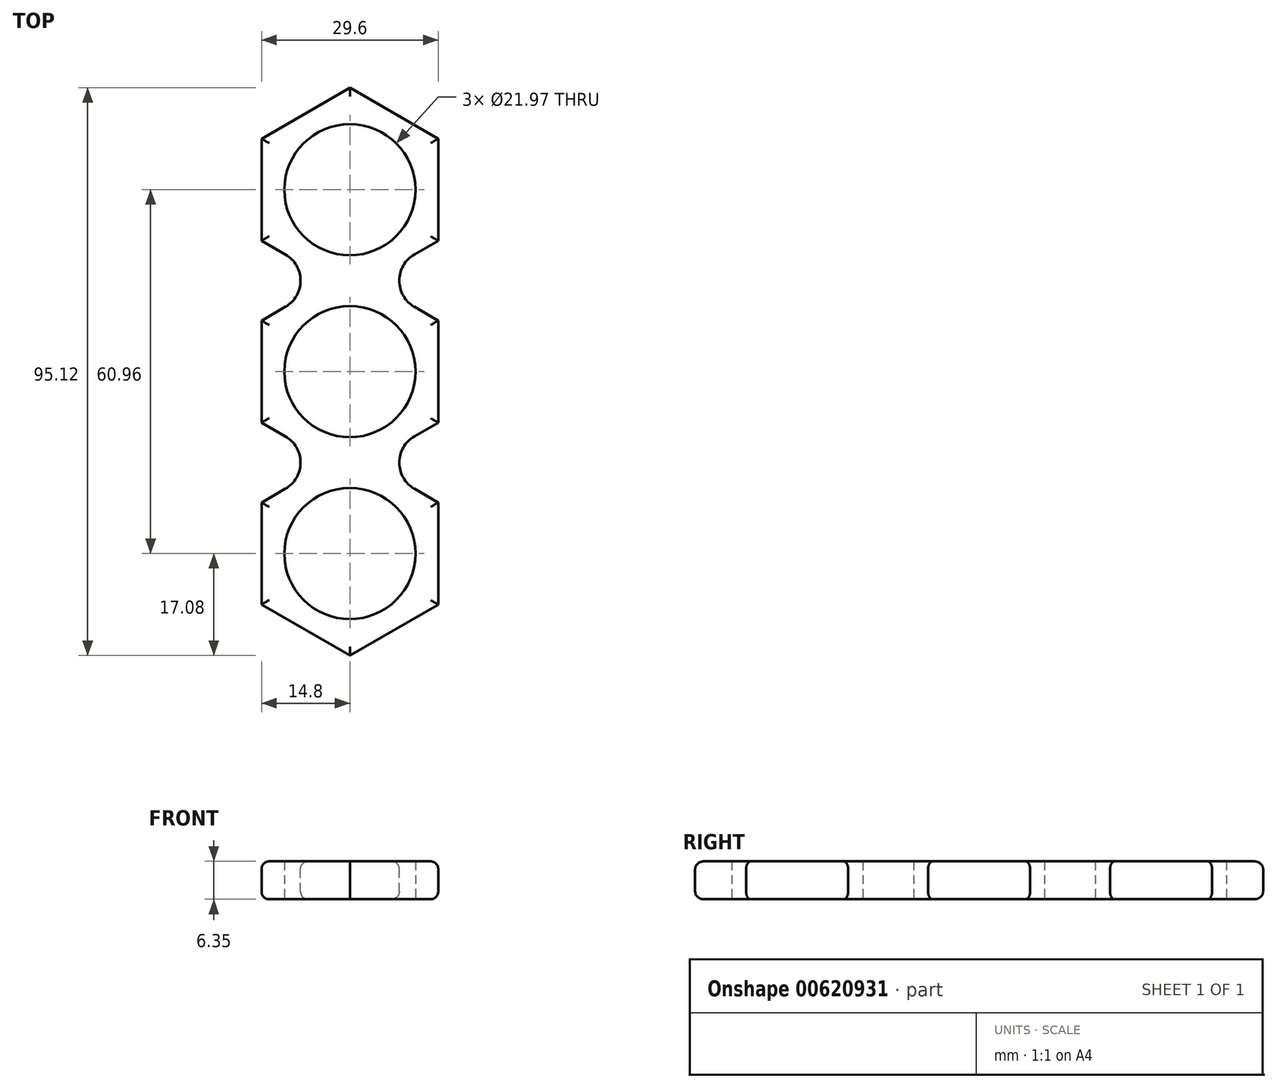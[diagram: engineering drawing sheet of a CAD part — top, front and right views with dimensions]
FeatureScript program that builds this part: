
annotation { "Feature Type Name" : "Feature", "Feature Type Description" : "" }
export const myFeature = defineFeature(function(context is Context, id is Id, definition is map)
    precondition{}
    {
        {
            var Q0;
            Q0=qCreatedBy(makeId("Top.planeOp"),FACE);
            var sketch = newSketch(context, id + "F0", { "sketchPlane" : qUnion([Q0])});
            skCircle(sketch, "E0", {"center": v(0, 0) * mm, "radius": 10.99 * mm});
            skCircle(sketch, "E1", {"center": v(0, 30.48) * mm, "radius": 10.99 * mm});
            skCircle(sketch, "E2", {"center": v(0, -30.48) * mm, "radius": 10.99 * mm});
            skCircle(sketch, "E3", {"center": v(0, -30.48) * mm, "radius": 14.8 * mm});
            skCircle(sketch, "E4", {"center": v(0, 30.48) * mm, "radius": 14.8 * mm});
            skLineSegment(sketch, "E5", {"start": v(0, 0) * mm, "end": v(0, 30.48) * mm});
            skLineSegment(sketch, "E6", {"start": v(0, 0) * mm, "end": v(0, -30.48) * mm});
            skCircle(sketch, "E7", {"center": v(0, 0) * mm, "radius": 14.8 * mm});
            skCircle(sketch, "E8.cCircle", {"center": v(0, 30.48) * mm, "radius": 14.8 * mm, "construction": true});
            skLineSegment(sketch, "E8.0", {"start": v(14.8, 39.02) * mm, "end": v(14.8, 21.94) * mm});
            skLineSegment(sketch, "E8.1", {"start": v(14.8, 21.94) * mm, "end": v(0, 13.4) * mm});
            skLineSegment(sketch, "E8.2", {"start": v(0, 13.4) * mm, "end": v(-14.8, 21.94) * mm});
            skLineSegment(sketch, "E8.3", {"start": v(-14.8, 21.94) * mm, "end": v(-14.8, 39.02) * mm});
            skLineSegment(sketch, "E8.4", {"start": v(-14.8, 39.02) * mm, "end": v(0, 47.56) * mm});
            skLineSegment(sketch, "E8.5", {"start": v(0, 47.56) * mm, "end": v(14.8, 39.02) * mm});
            skPoint(sketch, "E8.0.midPoint", {"position": v(14.8, 30.48) * mm});
            skCircle(sketch, "E9.cCircle", {"center": v(0, 0) * mm, "radius": 14.8 * mm, "construction": true});
            skLineSegment(sketch, "E9.0", {"start": v(14.8, 8.54) * mm, "end": v(14.8, -8.54) * mm});
            skLineSegment(sketch, "E9.1", {"start": v(14.8, -8.54) * mm, "end": v(0, -17.08) * mm});
            skLineSegment(sketch, "E9.2", {"start": v(0, -17.08) * mm, "end": v(-14.8, -8.54) * mm});
            skLineSegment(sketch, "E9.3", {"start": v(-14.8, -8.54) * mm, "end": v(-14.8, 8.54) * mm});
            skLineSegment(sketch, "E9.4", {"start": v(-14.8, 8.54) * mm, "end": v(0, 17.08) * mm});
            skLineSegment(sketch, "E9.5", {"start": v(0, 17.08) * mm, "end": v(14.8, 8.54) * mm});
            skPoint(sketch, "E9.0.midPoint", {"position": v(14.8, 0) * mm});
            skCircle(sketch, "E10.cCircle", {"center": v(0, -30.48) * mm, "radius": 14.8 * mm, "construction": true});
            skLineSegment(sketch, "E10.0", {"start": v(14.8, -21.94) * mm, "end": v(14.8, -39.02) * mm});
            skLineSegment(sketch, "E10.1", {"start": v(14.8, -39.02) * mm, "end": v(0, -47.56) * mm});
            skLineSegment(sketch, "E10.2", {"start": v(0, -47.56) * mm, "end": v(-14.8, -39.02) * mm});
            skLineSegment(sketch, "E10.3", {"start": v(-14.8, -39.02) * mm, "end": v(-14.8, -21.94) * mm});
            skLineSegment(sketch, "E10.4", {"start": v(-14.8, -21.94) * mm, "end": v(0, -13.4) * mm});
            skLineSegment(sketch, "E10.5", {"start": v(0, -13.4) * mm, "end": v(14.8, -21.94) * mm});
            skPoint(sketch, "E10.0.midPoint", {"position": v(14.8, -30.48) * mm});
            skSolve(sketch);
        }
        {
            var Q0;
            Q0 = qSketchRegion(id + "F0", true);
            var Q1;
            {var subQ0=sQuery(id+"F0.wireOp",EDGE,"E5");var subQ3=sQuery(id+"F0.wireOp",EDGE,"E0");var subQ4=makeQuery(id+"F0.imprint","INTERSECT",VERTEX,{"derivedFrom":[subQ3,subQ0]});Q1=makeQuery(id+"F0.imprint","IMPRINT",FACE,{"disambiguationData":[TD([[makeQuery(id+"F0.imprint","IMPRINT",EDGE,{"disambiguationData":[TD([[subQ4,1.0]])],"derivedFrom":subQ3}),-1.0]])]});}
            var Q2;
            {var subQ7=sQuery(id+"F0.wireOp",EDGE,"E0");var subQ11=sQuery(id+"F0.wireOp",EDGE,"E5");var subQ12=makeQuery(id+"F0.imprint","INTERSECT",VERTEX,{"derivedFrom":[subQ7,subQ11]});Q2=makeQuery(id+"F0.imprint","IMPRINT",FACE,{"disambiguationData":[TD([[makeQuery(id+"F0.imprint","IMPRINT",EDGE,{"disambiguationData":[TD([[subQ12,-1.0]])],"derivedFrom":subQ7}),-1.0]])]});}
            var Q3;
            {var subQ0=sQuery(id+"F0.wireOp",EDGE,"E9.4");var subQ1=sQuery(id+"F0.wireOp",EDGE,"E4");var subQ2=makeQuery(id+"F0.imprint","INTERSECT",VERTEX,{"derivedFrom":[subQ1,subQ0]});Q3=makeQuery(id+"F0.imprint","IMPRINT",FACE,{"disambiguationData":[TD([[makeQuery(id+"F0.imprint","IMPRINT",EDGE,{"disambiguationData":[TD([[subQ2,-1.0]])],"derivedFrom":subQ1}),1.0]])]});}
            var Q4;
            {var subQ0=sQuery(id+"F0.wireOp",EDGE,"E5");var subQ1=sQuery(id+"F0.wireOp",EDGE,"E4");var subQ2=makeQuery(id+"F0.imprint","INTERSECT",VERTEX,{"derivedFrom":[subQ1,subQ0]});Q4=makeQuery(id+"F0.imprint","IMPRINT",FACE,{"disambiguationData":[TD([[makeQuery(id+"F0.imprint","IMPRINT",EDGE,{"disambiguationData":[TD([[subQ2,-1.0]])],"derivedFrom":subQ1}),1.0]])]});}
            var Q5;
            {var subQ1=sQuery(id+"F0.wireOp",EDGE,"E5");var subQ3=sQuery(id+"F0.wireOp",EDGE,"E7");var subQ4=makeQuery(id+"F0.imprint","INTERSECT",VERTEX,{"derivedFrom":[subQ1,subQ3]});Q5=makeQuery(id+"F0.imprint","IMPRINT",FACE,{"disambiguationData":[TD([[makeQuery(id+"F0.imprint","IMPRINT",EDGE,{"disambiguationData":[TD([[subQ4,-1.0]])],"derivedFrom":subQ3}),1.0]])]});}
            var Q6;
            {var subQ1=sQuery(id+"F0.wireOp",EDGE,"E5");var subQ3=sQuery(id+"F0.wireOp",EDGE,"E7");var subQ4=makeQuery(id+"F0.imprint","INTERSECT",VERTEX,{"derivedFrom":[subQ1,subQ3]});Q6=makeQuery(id+"F0.imprint","IMPRINT",FACE,{"disambiguationData":[TD([[makeQuery(id+"F0.imprint","IMPRINT",EDGE,{"disambiguationData":[TD([[subQ4,1.0]])],"derivedFrom":subQ3}),1.0]])]});}
            var Q7;
            {var subQ0=sQuery(id+"F0.wireOp",EDGE,"E9.1");var subQ1=sQuery(id+"F0.wireOp",EDGE,"E3");var subQ2=makeQuery(id+"F0.imprint","INTERSECT",VERTEX,{"derivedFrom":[subQ1,subQ0]});Q7=makeQuery(id+"F0.imprint","IMPRINT",FACE,{"disambiguationData":[TD([[makeQuery(id+"F0.imprint","IMPRINT",EDGE,{"disambiguationData":[TD([[subQ2,-1.0]])],"derivedFrom":subQ1}),1.0]])]});}
            var Q8;
            {var subQ1=sQuery(id+"F0.wireOp",EDGE,"E6");var subQ3=sQuery(id+"F0.wireOp",EDGE,"E7");var subQ4=makeQuery(id+"F0.imprint","INTERSECT",VERTEX,{"derivedFrom":[subQ1,subQ3]});Q8=makeQuery(id+"F0.imprint","IMPRINT",FACE,{"disambiguationData":[TD([[makeQuery(id+"F0.imprint","IMPRINT",EDGE,{"disambiguationData":[TD([[subQ4,-1.0]])],"derivedFrom":subQ3}),1.0]])]});}
            var Q9;
            {var subQ1=sQuery(id+"F0.wireOp",EDGE,"E6");var subQ3=sQuery(id+"F0.wireOp",EDGE,"E7");var subQ4=makeQuery(id+"F0.imprint","INTERSECT",VERTEX,{"derivedFrom":[subQ1,subQ3]});Q9=makeQuery(id+"F0.imprint","IMPRINT",FACE,{"disambiguationData":[TD([[makeQuery(id+"F0.imprint","IMPRINT",EDGE,{"disambiguationData":[TD([[subQ4,1.0]])],"derivedFrom":subQ3}),1.0]])]});}
            var Q10;
            {var subQ0=sQuery(id+"F0.wireOp",EDGE,"E6");var subQ1=sQuery(id+"F0.wireOp",EDGE,"E3");var subQ2=makeQuery(id+"F0.imprint","INTERSECT",VERTEX,{"derivedFrom":[subQ1,subQ0]});Q10=makeQuery(id+"F0.imprint","IMPRINT",FACE,{"disambiguationData":[TD([[makeQuery(id+"F0.imprint","IMPRINT",EDGE,{"disambiguationData":[TD([[subQ2,-1.0]])],"derivedFrom":subQ1}),1.0]])]});}
            extrude(context, id + "F1", {"entities" : qUnion([Q0, Q1, Q2, Q3, Q4, Q5, Q6, Q7, Q8, Q9, Q10]), "depth" : 6.35 * mm, "offsetDistance" : 25.4 * mm});
        }
        {
            var Q0;
            Q0=makeQuery(id+"F1.opExtrude","SWEPT_EDGE",EDGE,{"disambiguationData":[OSD([sQuery(id+"F0.wireOp",EDGE,"E8.2"),sQuery(id+"F0.wireOp",EDGE,"E9.4")])]});
            var Q1;
            Q1=makeQuery(id+"F1.opExtrude","SWEPT_EDGE",EDGE,{"disambiguationData":[OSD([sQuery(id+"F0.wireOp",EDGE,"E9.2"),sQuery(id+"F0.wireOp",EDGE,"E10.4")])]});
            var Q2;
            Q2=makeQuery(id+"F1.opExtrude","SWEPT_EDGE",EDGE,{"disambiguationData":[OSD([sQuery(id+"F0.wireOp",EDGE,"E9.1"),sQuery(id+"F0.wireOp",EDGE,"E10.5")])]});
            var Q3;
            Q3=makeQuery(id+"F1.opExtrude","SWEPT_EDGE",EDGE,{"disambiguationData":[OSD([sQuery(id+"F0.wireOp",EDGE,"E8.1"),sQuery(id+"F0.wireOp",EDGE,"E9.5")])]});
            fillet(context, id + "F2", {"entities" : qUnion([Q0, Q1, Q2, Q3]), "radius" : 5.08 * mm, "tangentPropagation" : true, "allowEdgeOverflow" : false});
        }
        {
            var Q0;
            Q0=makeQuery(id+"F1.opExtrude","CAP_EDGE",EDGE,{"disambiguationData":[OSD([sQuery(id+"F0.wireOp",EDGE,"E8.3")])],"isStart":false});
            var Q1;
            Q1=makeQuery(id+"F1.opExtrude","CAP_EDGE",EDGE,{"disambiguationData":[OSD([sQuery(id+"F0.wireOp",EDGE,"E8.4")])],"isStart":false});
            var Q2;
            Q2=makeQuery(id+"F1.opExtrude","CAP_EDGE",EDGE,{"disambiguationData":[OSD([sQuery(id+"F0.wireOp",EDGE,"E8.5")])],"isStart":false});
            var Q3;
            Q3=makeQuery(id+"F1.opExtrude","CAP_EDGE",EDGE,{"disambiguationData":[OSD([sQuery(id+"F0.wireOp",EDGE,"E8.0")])],"isStart":false});
            var Q4;
            Q4=makeQuery(id+"F1.opExtrude","CAP_EDGE",EDGE,{"disambiguationData":[OSD([sQuery(id+"F0.wireOp",EDGE,"E8.1")])],"isStart":false});
            var Q5;
            Q5=makeQuery(id+"F1.opExtrude","CAP_EDGE",EDGE,{"disambiguationData":[OSD([sQuery(id+"F0.wireOp",EDGE,"E8.2")])],"isStart":false});
            var Q6;
            Q6=makeQuery(id+"F1.opExtrude","CAP_EDGE",EDGE,{"disambiguationData":[OSD([sQuery(id+"F0.wireOp",EDGE,"E9.5")])],"isStart":false});
            var Q7;
            Q7=makeQuery(id+"F1.opExtrude","CAP_EDGE",EDGE,{"disambiguationData":[OSD([sQuery(id+"F0.wireOp",EDGE,"E9.0")])],"isStart":false});
            var Q8;
            Q8=makeQuery(id+"F1.opExtrude","CAP_EDGE",EDGE,{"disambiguationData":[OSD([sQuery(id+"F0.wireOp",EDGE,"E9.1")])],"isStart":false});
            var Q9;
            Q9=makeQuery(id+"F1.opExtrude","CAP_EDGE",EDGE,{"disambiguationData":[OSD([sQuery(id+"F0.wireOp",EDGE,"E10.5")])],"isStart":false});
            var Q10;
            Q10=makeQuery(id+"F1.opExtrude","CAP_EDGE",EDGE,{"disambiguationData":[OSD([sQuery(id+"F0.wireOp",EDGE,"E10.0")])],"isStart":false});
            var Q11;
            Q11=makeQuery(id+"F1.opExtrude","CAP_EDGE",EDGE,{"disambiguationData":[OSD([sQuery(id+"F0.wireOp",EDGE,"E10.1")])],"isStart":false});
            var Q12;
            Q12=makeQuery(id+"F1.opExtrude","CAP_EDGE",EDGE,{"disambiguationData":[OSD([sQuery(id+"F0.wireOp",EDGE,"E10.2")])],"isStart":false});
            var Q13;
            Q13=makeQuery(id+"F1.opExtrude","CAP_EDGE",EDGE,{"disambiguationData":[OSD([sQuery(id+"F0.wireOp",EDGE,"E10.3")])],"isStart":false});
            var Q14;
            Q14=makeQuery(id+"F1.opExtrude","CAP_EDGE",EDGE,{"disambiguationData":[OSD([sQuery(id+"F0.wireOp",EDGE,"E10.4")])],"isStart":false});
            var Q15;
            Q15=makeQuery(id+"F1.opExtrude","CAP_EDGE",EDGE,{"disambiguationData":[OSD([sQuery(id+"F0.wireOp",EDGE,"E9.2")])],"isStart":false});
            var Q16;
            Q16=makeQuery(id+"F1.opExtrude","CAP_EDGE",EDGE,{"disambiguationData":[OSD([sQuery(id+"F0.wireOp",EDGE,"E9.3")])],"isStart":false});
            var Q17;
            Q17=makeQuery(id+"F1.opExtrude","CAP_EDGE",EDGE,{"disambiguationData":[OSD([sQuery(id+"F0.wireOp",EDGE,"E9.4")])],"isStart":false});
            fillet(context, id + "F3", {"entities" : qUnion([Q0, Q1, Q2, Q3, Q4, Q5, Q6, Q7, Q8, Q9, Q10, Q11, Q12, Q13, Q14, Q15, Q16, Q17]), "radius" : 1.27 * mm, "tangentPropagation" : true, "allowEdgeOverflow" : false});
        }
        {
            var Q0;
            Q0=makeQuery(id+"F1.opExtrude","CAP_EDGE",EDGE,{"disambiguationData":[OSD([sQuery(id+"F0.wireOp",EDGE,"E8.3")])],"isStart":true});
            var Q1;
            Q1=makeQuery(id+"F1.opExtrude","CAP_EDGE",EDGE,{"disambiguationData":[OSD([sQuery(id+"F0.wireOp",EDGE,"E8.4")])],"isStart":true});
            var Q2;
            Q2=makeQuery(id+"F1.opExtrude","CAP_EDGE",EDGE,{"disambiguationData":[OSD([sQuery(id+"F0.wireOp",EDGE,"E8.5")])],"isStart":true});
            var Q3;
            Q3=makeQuery(id+"F1.opExtrude","CAP_EDGE",EDGE,{"disambiguationData":[OSD([sQuery(id+"F0.wireOp",EDGE,"E8.0")])],"isStart":true});
            var Q4;
            Q4=makeQuery(id+"F1.opExtrude","CAP_EDGE",EDGE,{"disambiguationData":[OSD([sQuery(id+"F0.wireOp",EDGE,"E8.1")])],"isStart":true});
            var Q5;
            Q5=makeQuery(id+"F1.opExtrude","CAP_EDGE",EDGE,{"disambiguationData":[OSD([sQuery(id+"F0.wireOp",EDGE,"E8.2")])],"isStart":true});
            var Q6;
            Q6=makeQuery(id+"F1.opExtrude","CAP_EDGE",EDGE,{"disambiguationData":[OSD([sQuery(id+"F0.wireOp",EDGE,"E9.4")])],"isStart":true});
            var Q7;
            Q7=makeQuery(id+"F1.opExtrude","CAP_EDGE",EDGE,{"disambiguationData":[OSD([sQuery(id+"F0.wireOp",EDGE,"E9.5")])],"isStart":true});
            var Q8;
            Q8=makeQuery(id+"F1.opExtrude","CAP_EDGE",EDGE,{"disambiguationData":[OSD([sQuery(id+"F0.wireOp",EDGE,"E9.0")])],"isStart":true});
            var Q9;
            Q9=makeQuery(id+"F1.opExtrude","CAP_EDGE",EDGE,{"disambiguationData":[OSD([sQuery(id+"F0.wireOp",EDGE,"E9.1")])],"isStart":true});
            var Q10;
            Q10=makeQuery(id+"F1.opExtrude","CAP_EDGE",EDGE,{"disambiguationData":[OSD([sQuery(id+"F0.wireOp",EDGE,"E9.2")])],"isStart":true});
            var Q11;
            Q11=makeQuery(id+"F1.opExtrude","CAP_EDGE",EDGE,{"disambiguationData":[OSD([sQuery(id+"F0.wireOp",EDGE,"E9.3")])],"isStart":true});
            var Q12;
            Q12=makeQuery(id+"F1.opExtrude","CAP_EDGE",EDGE,{"disambiguationData":[OSD([sQuery(id+"F0.wireOp",EDGE,"E10.4")])],"isStart":true});
            var Q13;
            Q13=makeQuery(id+"F1.opExtrude","CAP_EDGE",EDGE,{"disambiguationData":[OSD([sQuery(id+"F0.wireOp",EDGE,"E10.5")])],"isStart":true});
            var Q14;
            Q14=makeQuery(id+"F1.opExtrude","CAP_EDGE",EDGE,{"disambiguationData":[OSD([sQuery(id+"F0.wireOp",EDGE,"E10.0")])],"isStart":true});
            var Q15;
            Q15=makeQuery(id+"F1.opExtrude","CAP_EDGE",EDGE,{"disambiguationData":[OSD([sQuery(id+"F0.wireOp",EDGE,"E10.1")])],"isStart":true});
            var Q16;
            Q16=makeQuery(id+"F1.opExtrude","CAP_EDGE",EDGE,{"disambiguationData":[OSD([sQuery(id+"F0.wireOp",EDGE,"E10.2")])],"isStart":true});
            var Q17;
            Q17=makeQuery(id+"F1.opExtrude","CAP_EDGE",EDGE,{"disambiguationData":[OSD([sQuery(id+"F0.wireOp",EDGE,"E10.3")])],"isStart":true});
            fillet(context, id + "F4", {"entities" : qUnion([Q0, Q1, Q2, Q3, Q4, Q5, Q6, Q7, Q8, Q9, Q10, Q11, Q12, Q13, Q14, Q15, Q16, Q17]), "radius" : 1.27 * mm, "tangentPropagation" : true, "allowEdgeOverflow" : false});
        }
    });
